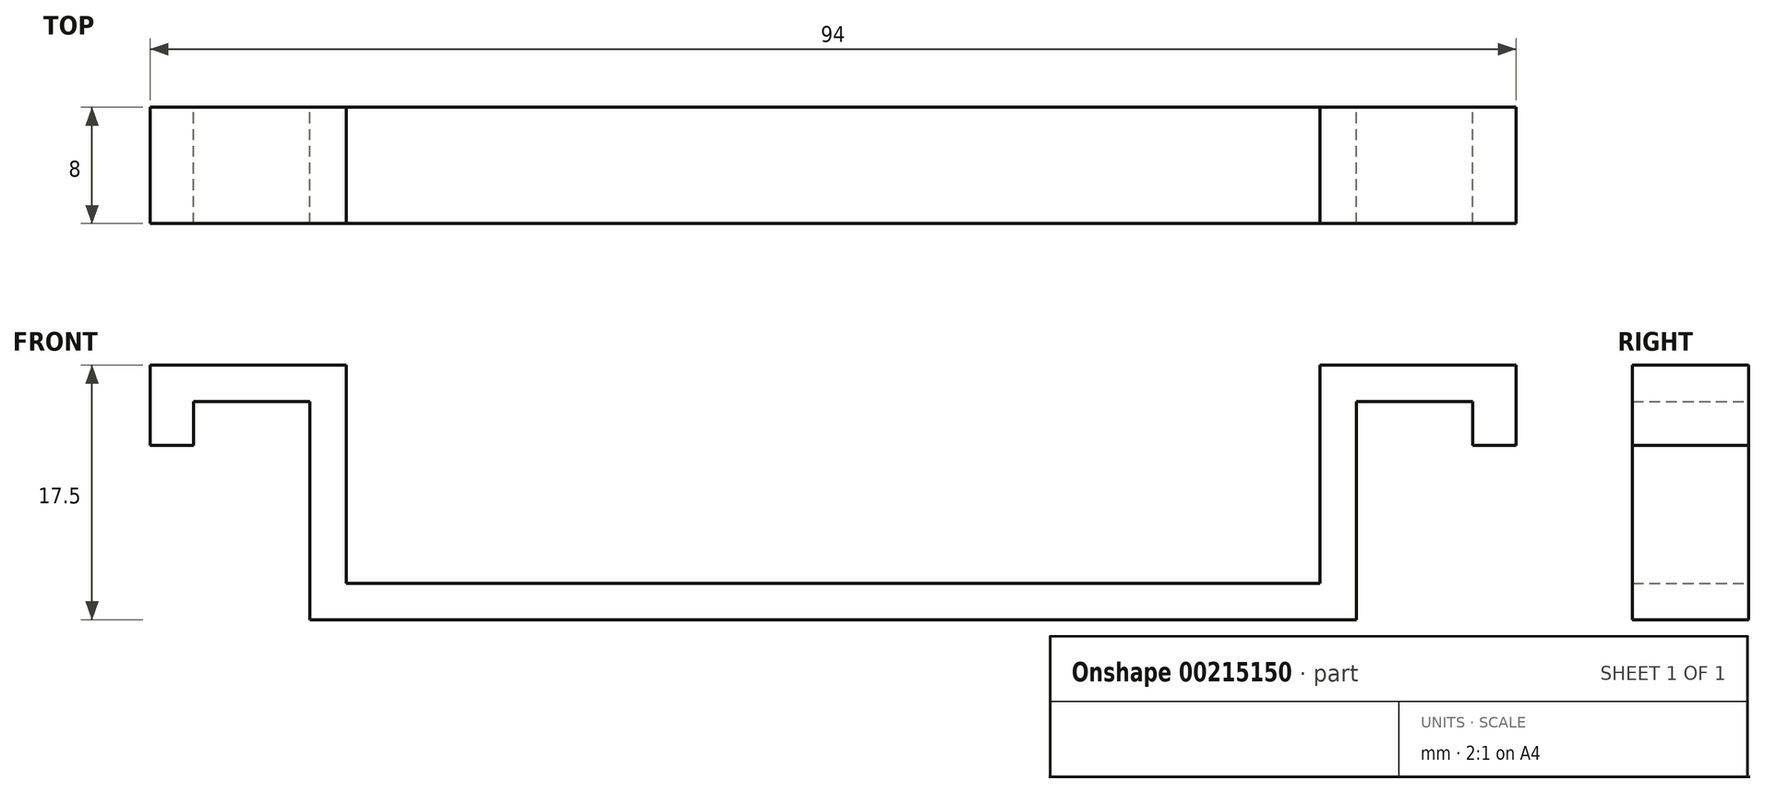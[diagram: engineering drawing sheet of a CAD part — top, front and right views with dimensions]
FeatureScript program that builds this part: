
annotation { "Feature Type Name" : "Feature", "Feature Type Description" : "" }
export const myFeature = defineFeature(function(context is Context, id is Id, definition is map)
    precondition{}
    {
        {
            var Q0;
            Q0=qCreatedBy(makeId("Front.planeOp"),FACE);
            var sketch = newSketch(context, id + "F0", { "sketchPlane" : qUnion([Q0])});
            skLineSegment(sketch, "E0", {"start": v(-47, 0) * mm, "end": v(-33.5, 0) * mm});
            skLineSegment(sketch, "E1", {"start": v(-33.5, 0) * mm, "end": v(-33.5, -15) * mm});
            skLineSegment(sketch, "E2", {"start": v(-33.5, -15) * mm, "end": v(0, -15) * mm});
            skLineSegment(sketch, "E3.0", {"start": v(-36, -17.5) * mm, "end": v(0, -17.5) * mm});
            skLineSegment(sketch, "E3.1", {"start": v(-36, -2.5) * mm, "end": v(-36, -17.5) * mm});
            skLineSegment(sketch, "E3.2", {"start": v(-47, -2.5) * mm, "end": v(-36, -2.5) * mm});
            skLineSegment(sketch, "E4", {"start": v(-47, 0) * mm, "end": v(-47, -5.5) * mm});
            skLineSegment(sketch, "E5", {"start": v(-47, -5.5) * mm, "end": v(-44, -5.5) * mm});
            skLineSegment(sketch, "E6", {"start": v(-44, -5.5) * mm, "end": v(-44, -2.5) * mm});
            skLineSegment(sketch, "E7", {"start": v(0, -15) * mm, "end": v(0, -17.5) * mm});
            skSolve(sketch);
        }
        {
            var Q0;
            Q0 = qSketchRegion(id + "F0", true);
            extrude(context, id + "F1", {"entities" : qUnion([Q0]), "endBound" : BoundingType.SYMMETRIC, "depth" : 8 * mm});
        }
        {
            var Q0;
            Q0=makeQuery(id+"F1.opExtrude","SWEPT_FACE",FACE,{"disambiguationData":[OSD([sQuery(id+"F0.wireOp",EDGE,"E2")])]});
            var sketch = newSketch(context, id + "F2", { "sketchPlane" : qUnion([Q0])});
            skLineSegment(sketch, "E8", {"start": v(-27.5, 0.5) * mm, "end": v(-27.5, -0.5) * mm, "construction": true});
            skArc(sketch, "E9.0.startCap", {"start": v(-31, 0.5) * mm, "mid": v(-27.5, 4) * mm, "end": v(-24, 0.5) * mm});
            skArc(sketch, "E9.0.endCap", {"start": v(-24, -0.5) * mm, "mid": v(-27.5, -4) * mm, "end": v(-31, -0.5) * mm});
            skLineSegment(sketch, "E9.0.left", {"start": v(-24, 0.5) * mm, "end": v(-24, -0.5) * mm});
            skLineSegment(sketch, "E9.0.right", {"start": v(-31, 0.5) * mm, "end": v(-31, -0.5) * mm});
            skSolve(sketch);
        }
        {
            var Q0;
            Q0=makeQuery(id+"F1.opExtrude","SWEPT_BODY",BODY,{"disambiguationData":[OSD([sQuery(id+"F0.wireOp",EDGE,"E0"),sQuery(id+"F0.wireOp",EDGE,"E1"),sQuery(id+"F0.wireOp",EDGE,"E2"),sQuery(id+"F0.wireOp",EDGE,"E3.0"),sQuery(id+"F0.wireOp",EDGE,"E3.1"),sQuery(id+"F0.wireOp",EDGE,"E3.2"),sQuery(id+"F0.wireOp",EDGE,"E4"),sQuery(id+"F0.wireOp",EDGE,"E5"),sQuery(id+"F0.wireOp",EDGE,"E6"),sQuery(id+"F0.wireOp",EDGE,"E7")])]});
            var Q1;
            Q1=qCreatedBy(makeId("Right.planeOp"),FACE);
            mirror(context, id + "F3", {"operationType" : NewBodyOperationType.ADD, "entities" : qUnion([Q0]), "mirrorPlane" : qUnion([Q1])});
        }
    });
